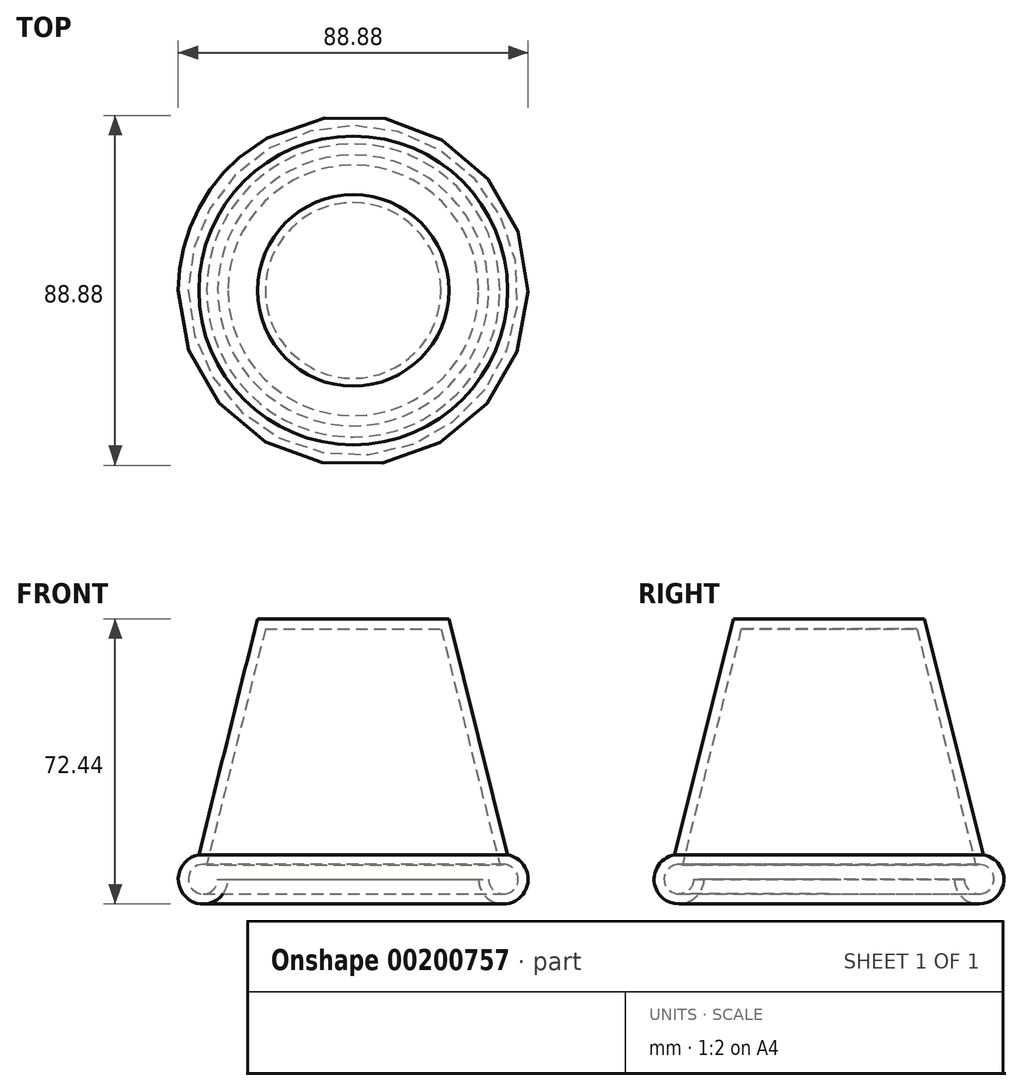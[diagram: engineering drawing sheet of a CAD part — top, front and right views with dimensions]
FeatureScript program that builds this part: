
annotation { "Feature Type Name" : "Feature", "Feature Type Description" : "" }
export const myFeature = defineFeature(function(context is Context, id is Id, definition is map)
    precondition{}
    {
        {
            var Q0;
            Q0=qCreatedBy(makeId("Front.planeOp"),FACE);
            var sketch = newSketch(context, id + "F0", { "sketchPlane" : qUnion([Q0])});
            skLineSegment(sketch, "E0", {"start": v(0, 0) * mm, "end": v(0, 63.6) * mm});
            skLineSegment(sketch, "E1", {"start": v(0, 0) * mm, "end": v(34.4, 0) * mm});
            skLineSegment(sketch, "E2", {"start": v(0, 63.6) * mm, "end": v(22.32, 63.6) * mm});
            skLineSegment(sketch, "E3", {"start": v(22.32, 63.6) * mm, "end": v(37.24, 3.64) * mm});
            skArc(sketch, "E4", {"start": v(34.4, 0) * mm, "mid": v(41.1, -2.31) * mm, "end": v(37.24, 3.64) * mm});
            skPoint(sketch, "E5.end.orphan", {"position": v(27.46, 56.02) * mm});
            skPoint(sketch, "E6.end.orphan", {"position": v(27.46, 44.2) * mm});
            skLineSegment(sketch, "E7", {"start": v(30.48, 56.02) * mm, "end": v(30.48, 46) * mm});
            skPoint(sketch, "E8.start.orphan", {"position": v(24.2, 56.02) * mm});
            skPoint(sketch, "E9.end.orphan", {"position": v(27.46, 46) * mm});
            skLineSegment(sketch, "E10", {"start": v(24.2, 56.02) * mm, "end": v(30.48, 56.02) * mm});
            skLineSegment(sketch, "E11", {"start": v(26.7, 46) * mm, "end": v(30.48, 46) * mm});
            skSolve(sketch);
        }
        {
            var Q0;
            Q0=makeQuery(id+"F0.imprint","IMPRINT",FACE,{"disambiguationData":[TD([[makeQuery(id+"F0.imprint","IMPRINT",EDGE,{"derivedFrom":sQuery(id+"F0.wireOp",EDGE,"E0")}),-1.0]])]});
            var Q1;
            Q1=sQuery(id+"F0.wireOp",EDGE,"E7");
            var Q2;
            Q2=sQuery(id+"F0.wireOp",EDGE,"E10");
            var Q3;
            Q3=sQuery(id+"F0.wireOp",EDGE,"E11");
            var Q4;
            Q4=sQuery(id+"F0.wireOp",EDGE,"E0");
            revolve(context, id + "F1", {"bodyType" : ToolBodyType.SURFACE, "entities" : qUnion([Q0]), "surfaceEntities" : qUnion([Q1, Q2, Q3]), "axis" : qUnion([Q4]), "revolveType" : RevolveType.FULL});
        }
        {
            var Q0;
            Q0=makeQuery(id+"F0.imprint","IMPRINT",FACE,{"disambiguationData":[TD([[makeQuery(id+"F0.imprint","IMPRINT",EDGE,{"derivedFrom":sQuery(id+"F0.wireOp",EDGE,"E0")}),-1.0]])]});
            var Q1;
            Q1=sQuery(id+"F0.wireOp",EDGE,"E0");
            revolve(context, id + "F2", {"entities" : qUnion([Q0]), "axis" : qUnion([Q1]), "revolveType" : RevolveType.FULL});
        }
        {
            var Q0;
            Q0=makeQuery(id+"F2.opRevolve","SWEPT_FACE",FACE,{"disambiguationData":[OSD([sQuery(id+"F0.wireOp",EDGE,"E1")])]});
            shell(context, id + "F3", {"entities" : qUnion([Q0]), "thickness" : 2.54 * mm, "oppositeDirection" : true});
        }
    });
